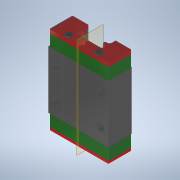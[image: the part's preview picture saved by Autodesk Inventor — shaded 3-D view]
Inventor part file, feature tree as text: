
AUTODESK INVENTOR PART (.ipt)
format: ipt  version: 2022 (Build 260153000, 153)  size: 496,640 bytes
history: imported  units: mm
features: plane x1, other x1, imported_body x1
ambient origin geometry x8: Origin, YZ Plane, XZ Plane, XY Plane, X Axis, Y Axis, Z Axis, Center Point
bodies: Volumenkörper1 (imported_parasolid)
feature tree (3):
  plane  "Arbeitsebene1"
  other  "Импортированный1"
  imported_body  NMx_Import_Brep_tag  [imported B-rep: ~66 faces, bbox_mm=[16.25, 28.4, 7.108885]]
